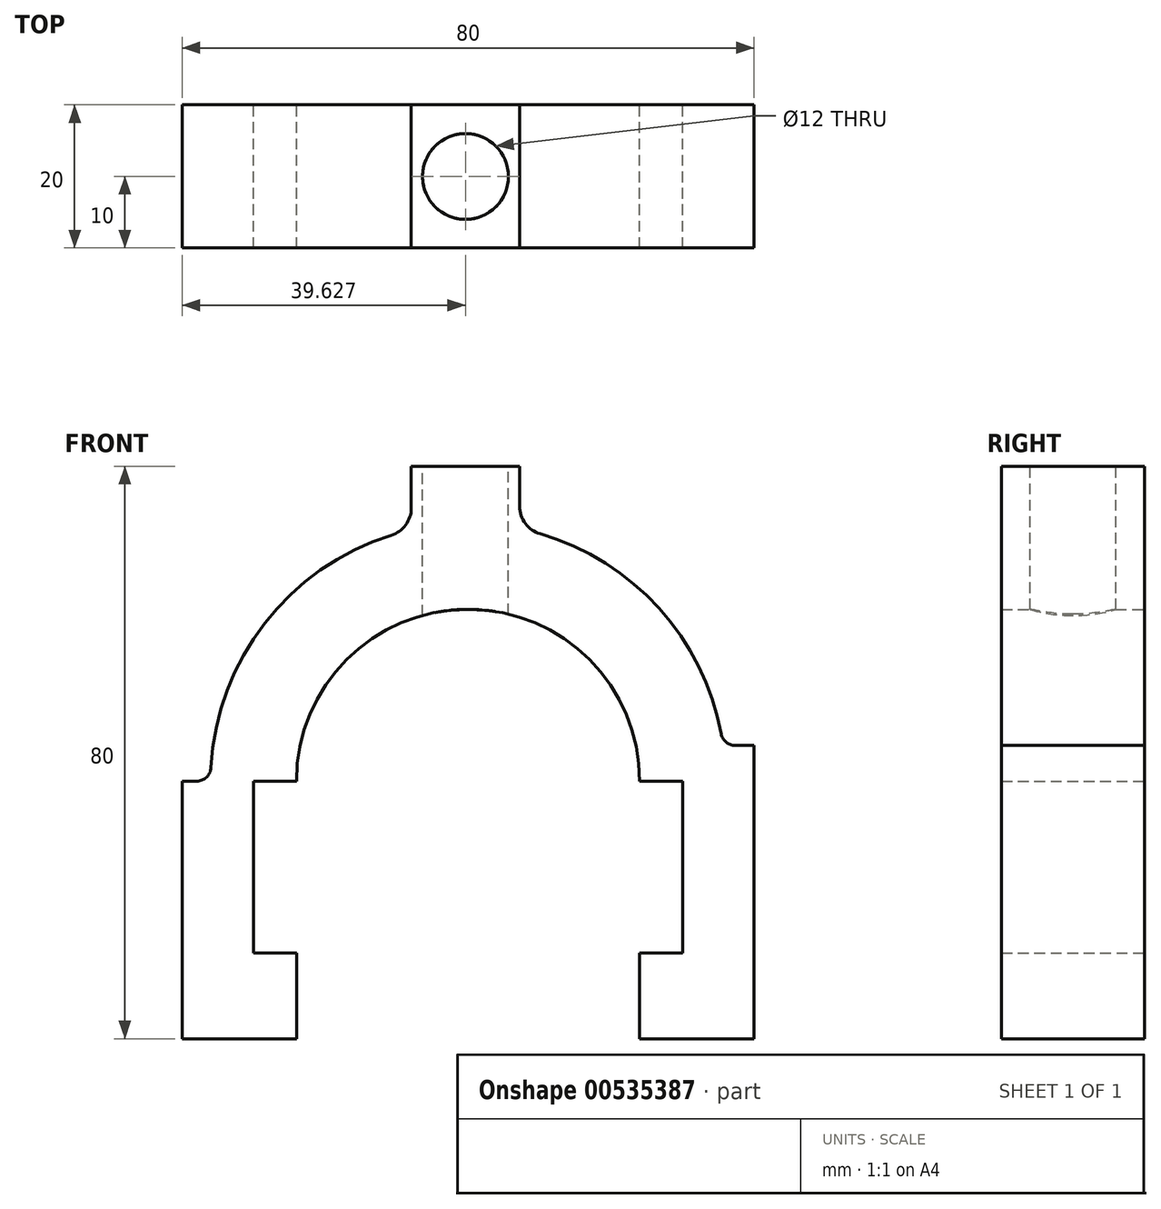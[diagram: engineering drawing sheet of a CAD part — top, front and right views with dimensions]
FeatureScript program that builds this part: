
annotation { "Feature Type Name" : "Feature", "Feature Type Description" : "" }
export const myFeature = defineFeature(function(context is Context, id is Id, definition is map)
    precondition{}
    {
        {
            var Q0;
            Q0=qCreatedBy(makeId("Front.planeOp"),FACE);
            var sketch = newSketch(context, id + "F0", { "sketchPlane" : qUnion([Q0])});
            skLineSegment(sketch, "E0.bottom", {"start": v(-37, 11.64) * mm, "end": v(-34.95, 11.64) * mm});
            skLineSegment(sketch, "E0.left", {"start": v(-37, 11.64) * mm, "end": v(-37, -24.36) * mm});
            skLineSegment(sketch, "E1", {"start": v(-37, -24.36) * mm, "end": v(-21, -24.36) * mm});
            skLineSegment(sketch, "E2", {"start": v(-21, -24.36) * mm, "end": v(-21, -12.36) * mm});
            skLineSegment(sketch, "E3", {"start": v(-21, -12.36) * mm, "end": v(-27, -12.36) * mm});
            skLineSegment(sketch, "E4", {"start": v(-27, -12.36) * mm, "end": v(-27, 11.64) * mm});
            skLineSegment(sketch, "E5.MirrorCS", {"start": v(27, -12.36) * mm, "end": v(33, -12.36) * mm});
            skLineSegment(sketch, "E6.MirrorCS", {"start": v(43, 16.62) * mm, "end": v(40.35, 16.62) * mm});
            skLineSegment(sketch, "E7.MirrorCS", {"start": v(43, -24.36) * mm, "end": v(27, -24.36) * mm});
            skLineSegment(sketch, "E8.MirrorCS", {"start": v(33, -12.36) * mm, "end": v(33, 11.64) * mm});
            skLineSegment(sketch, "E9.MirrorCS", {"start": v(27, -24.36) * mm, "end": v(27, -12.36) * mm});
            skLineSegment(sketch, "E10.MirrorCS", {"start": v(43, 16.62) * mm, "end": v(43, -24.36) * mm});
            skLineSegment(sketch, "E11", {"start": v(-27, 11.64) * mm, "end": v(-21, 11.64) * mm});
            skArc(sketch, "E12", {"start": v(-7.76, 46) * mm, "mid": v(-25.44, 33.71) * mm, "end": v(-32.95, 13.53) * mm});
            skArc(sketch, "E13", {"start": v(38.39, 18.25) * mm, "mid": v(29.69, 35.8) * mm, "end": v(13.08, 46.2) * mm});
            skLineSegment(sketch, "E14", {"start": v(-4.95, 49.81) * mm, "end": v(-4.95, 55.64) * mm});
            skLineSegment(sketch, "E15", {"start": v(-4.95, 55.64) * mm, "end": v(10.2, 55.64) * mm});
            skLineSegment(sketch, "E16", {"start": v(10.2, 55.64) * mm, "end": v(10.2, 50.04) * mm});
            skPoint(sketch, "E17", {"position": v(2.63, 55.64) * mm});
            skPoint(sketch, "E18.visualSharp", {"position": v(-33, 11.64) * mm});
            skArc(sketch, "E18.filletArc", {"start": v(-34.95, 11.64) * mm, "mid": v(-33.57, 12.19) * mm, "end": v(-32.95, 13.53) * mm});
            skPoint(sketch, "E19.visualSharp", {"position": v(38.65, 16.62) * mm});
            skArc(sketch, "E19.filletArc", {"start": v(38.39, 18.25) * mm, "mid": v(39.07, 17.08) * mm, "end": v(40.35, 16.62) * mm});
            skArc(sketch, "E20", {"start": v(27, 11.64) * mm, "mid": v(3, 35.64) * mm, "end": v(-21, 11.64) * mm});
            skLineSegment(sketch, "E21.trimOffspring", {"start": v(27, 11.64) * mm, "end": v(33, 11.64) * mm});
            skPoint(sketch, "E22.orphan", {"position": v(2.63, 47.64) * mm});
            skPoint(sketch, "E23.visualSharp", {"position": v(-4.95, 46.75) * mm});
            skArc(sketch, "E23.filletArc", {"start": v(-7.76, 46) * mm, "mid": v(-5.73, 47.45) * mm, "end": v(-4.95, 49.81) * mm});
            skPoint(sketch, "E24.visualSharp", {"position": v(10.2, 46.91) * mm});
            skArc(sketch, "E24.filletArc", {"start": v(10.2, 50.04) * mm, "mid": v(11, 47.64) * mm, "end": v(13.08, 46.2) * mm});
            skSolve(sketch);
        }
        {
            var Q0;
            Q0 = qSketchRegion(id + "F0", true);
            extrude(context, id + "F1", {"entities" : qUnion([Q0]), "depth" : 20 * mm, "offsetDistance" : 25 * mm});
        }
        {
            var Q0;
            Q0=makeQuery(id+"F1.opExtrude","SWEPT_FACE",FACE,{"disambiguationData":[OSD([sQuery(id+"F0.wireOp",EDGE,"E15")])]});
            var sketch = newSketch(context, id + "F2", { "sketchPlane" : qUnion([Q0])});
            skCircle(sketch, "E25", {"center": v(2.63, -10) * mm, "radius": 6 * mm});
            skPoint(sketch, "E25.centerSnap0", {"position": v(2.63, -20) * mm});
            skSolve(sketch);
        }
        {
            var Q0;
            Q0 = qSketchRegion(id + "F2", true);
            extrude(context, id + "F3", {"entities" : qUnion([Q0]), "operationType" : NewBodyOperationType.REMOVE, "endBound" : BoundingType.THROUGH_ALL, "oppositeDirection" : true, "depth" : 25 * mm, "offsetDistance" : 25 * mm});
        }
    });
